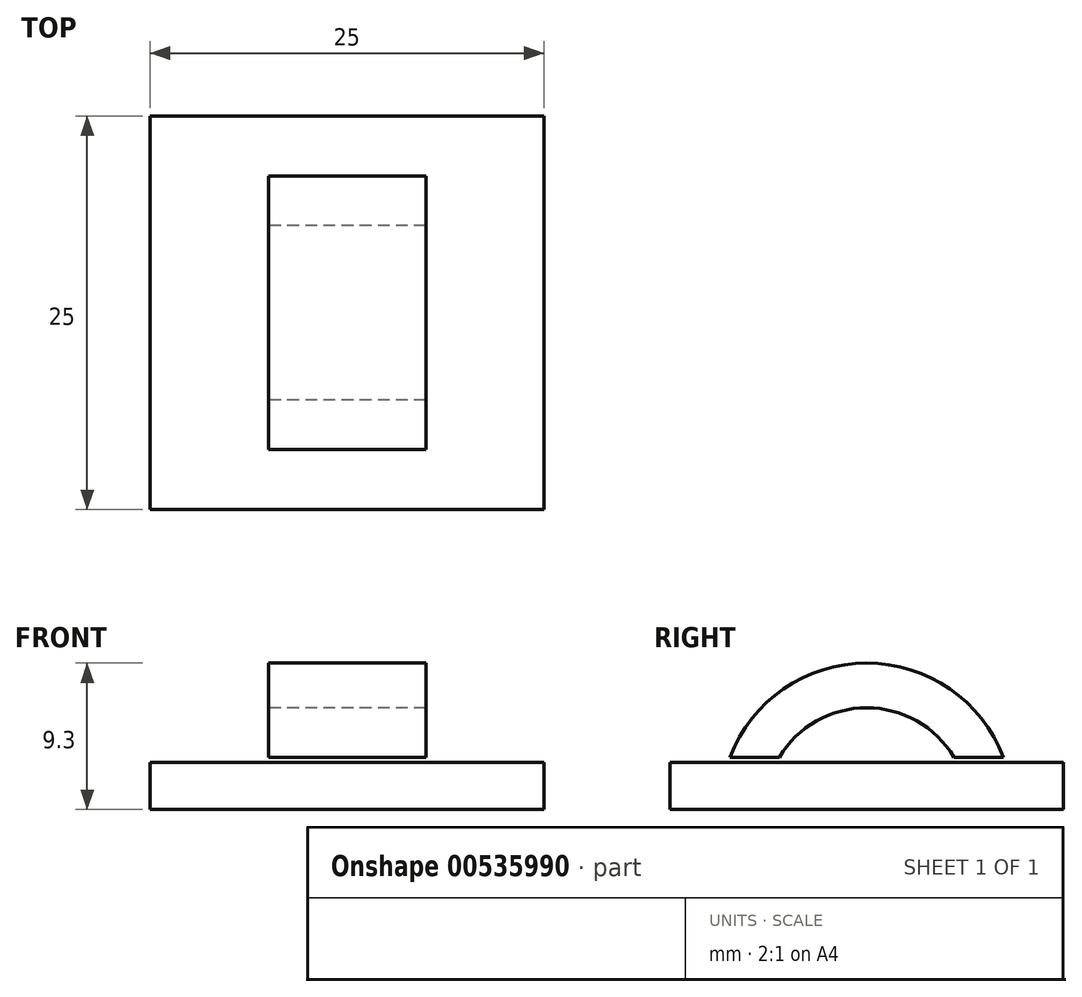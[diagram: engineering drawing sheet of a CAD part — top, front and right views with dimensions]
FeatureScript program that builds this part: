
annotation { "Feature Type Name" : "Feature", "Feature Type Description" : "" }
export const myFeature = defineFeature(function(context is Context, id is Id, definition is map)
    precondition{}
    {
        {
            var Q0;
            Q0=qCreatedBy(makeId("Top.planeOp"),FACE);
            var sketch = newSketch(context, id + "F0", { "sketchPlane" : qUnion([Q0])});
            skLineSegment(sketch, "E0.bottom", {"start": v(12.5, 12.5) * mm, "end": v(-12.5, 12.5) * mm});
            skLineSegment(sketch, "E0.top", {"start": v(12.5, -12.5) * mm, "end": v(-12.5, -12.5) * mm});
            skLineSegment(sketch, "E0.left", {"start": v(12.5, 12.5) * mm, "end": v(12.5, -12.5) * mm});
            skLineSegment(sketch, "E0.right", {"start": v(-12.5, 12.5) * mm, "end": v(-12.5, -12.5) * mm});
            skPoint(sketch, "E0.middle", {"position": v(0, 0) * mm});
            skSolve(sketch);
        }
        {
            var Q0;
            Q0 = qSketchRegion(id + "F0", true);
            extrude(context, id + "F1", {"entities" : qUnion([Q0]), "depth" : 3 * mm, "offsetDistance" : 25 * mm});
        }
        {
            var Q0;
            Q0=qCreatedBy(makeId("Right.planeOp"),FACE);
            var sketch = newSketch(context, id + "F2", { "sketchPlane" : qUnion([Q0])});
            skCircle(sketch, "E1", {"center": v(0, 0) * mm, "radius": 6.46 * mm});
            skCircle(sketch, "E2", {"center": v(0, 0) * mm, "radius": 9.3 * mm});
            skLineSegment(sketch, "E3", {"start": v(8.7, 3.32) * mm, "end": v(-8.7, 3.32) * mm});
            skSolve(sketch);
        }
        {
            var Q0;
            {var subQ0=sQuery(id+"F2.wireOp",EDGE,"E3");var subQ1=sQuery(id+"F2.wireOp",EDGE,"E1");var subQ2=makeQuery(id+"F2.imprint","INTERSECT",VERTEX,{"disambiguationData":[OD(0.0)],"derivedFrom":[subQ1,subQ0]});Q0=makeQuery(id+"F2.imprint","IMPRINT",FACE,{"disambiguationData":[TD([[makeQuery(id+"F2.imprint","IMPRINT",EDGE,{"disambiguationData":[TD([[subQ2,-1.0]])],"derivedFrom":subQ1}),-1.0]])]});}
            extrude(context, id + "F3", {"entities" : qUnion([Q0]), "endBound" : BoundingType.SYMMETRIC, "depth" : 10 * mm, "offsetDistance" : 25 * mm});
        }
    });
